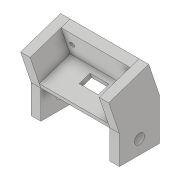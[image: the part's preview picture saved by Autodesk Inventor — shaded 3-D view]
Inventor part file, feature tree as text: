
AUTODESK INVENTOR PART (.ipt)
format: ipt  version: 2018.3 (Build 223284000, 284)  size: 232,448 bytes
history: native  units: in
note: dims shown in document units (in); Inventor stores cm internally (conversion verified against a paired STEP export)
features: extrude x13, sketch x5, plane x1
ambient origin geometry x8: Origin, YZ Plane, XZ Plane, XY Plane, X Axis, Y Axis, Z Axis, Center Point
bodies: Body1 (feature_tree)
feature tree (19):
  extrude  "Extrusion6"  Depth=0.25in TaperAngle=0.0deg
  extrude  "Extrusion8"  Depth=0.5in
  extrude  "Extrusion10"  Depth=0.65in
  extrude  "Extrusion11"  Depth=1.8in TaperAngle=0.0deg
  extrude  "Extrusion12"  TaperAngle=0.0deg  [1 undecoded]
  extrude  "Extrusion13"  TaperAngle=0.0deg  [1 undecoded]
  extrude  "Extrusion14"  Depth=1.1in
  extrude  "Extrusion15"  TaperAngle=0.0deg  [1 undecoded]
  extrude  "Extrusion16"  Depth=0.25in TaperAngle=0.0deg
  plane  "Work Plane1"
  extrude  "Extrusion24"  Depth=0.125in TaperAngle=0.0deg
  extrude  "Extrusion25"  Depth=0.125in TaperAngle=0.0deg
  extrude  "Extrusion26"  Depth=1.8in TaperAngle=0.0deg
  extrude  "Extrusion27"  Depth=1.8in TaperAngle=0.0deg
  sketch  "Sketch20"  dims[d40=1.8in d41=0.0in d50=0.25in d51=0.0in]
  sketch  "Sketch21"  dims[d55=0.3in d56=0.5in]
  sketch  "Sketch22"  dims[d57=0.65in d58=0.65in]
  sketch  "Sketch33"  dims[d59=1.0in d60=0.0in d62=1.8in d63=0.0in]
  sketch  "Sketch34"  dims[d67=0.25in d69=0.0in d70=0.0in d73=1.1in d76=0.0in d77=0.25in d78=0.0in d79=0.125in d80=0.0in d81=0.125in d82=0.0in d83=1.8in d84=0.0in d85=1.8in d86=0.0in d87=0.75in d88=0.75in d100=-0.1274in d132=0.375in d133=1.0in d134=0.0in d135=1.0in d136=0.0in d137=1.0in d138=0.0in d139=0.75in d144=0.26in d145=0.3667in d146=0.5215in d147=1.0in d148=0.0in d149=0.8503in d150=0.125in d151=0.1318in]
note: 3 required parameter values undecoded (feature->parameter linkage not recoverable at this tier; creation-order binding heuristic only, values carry confidence <= 0.55)
